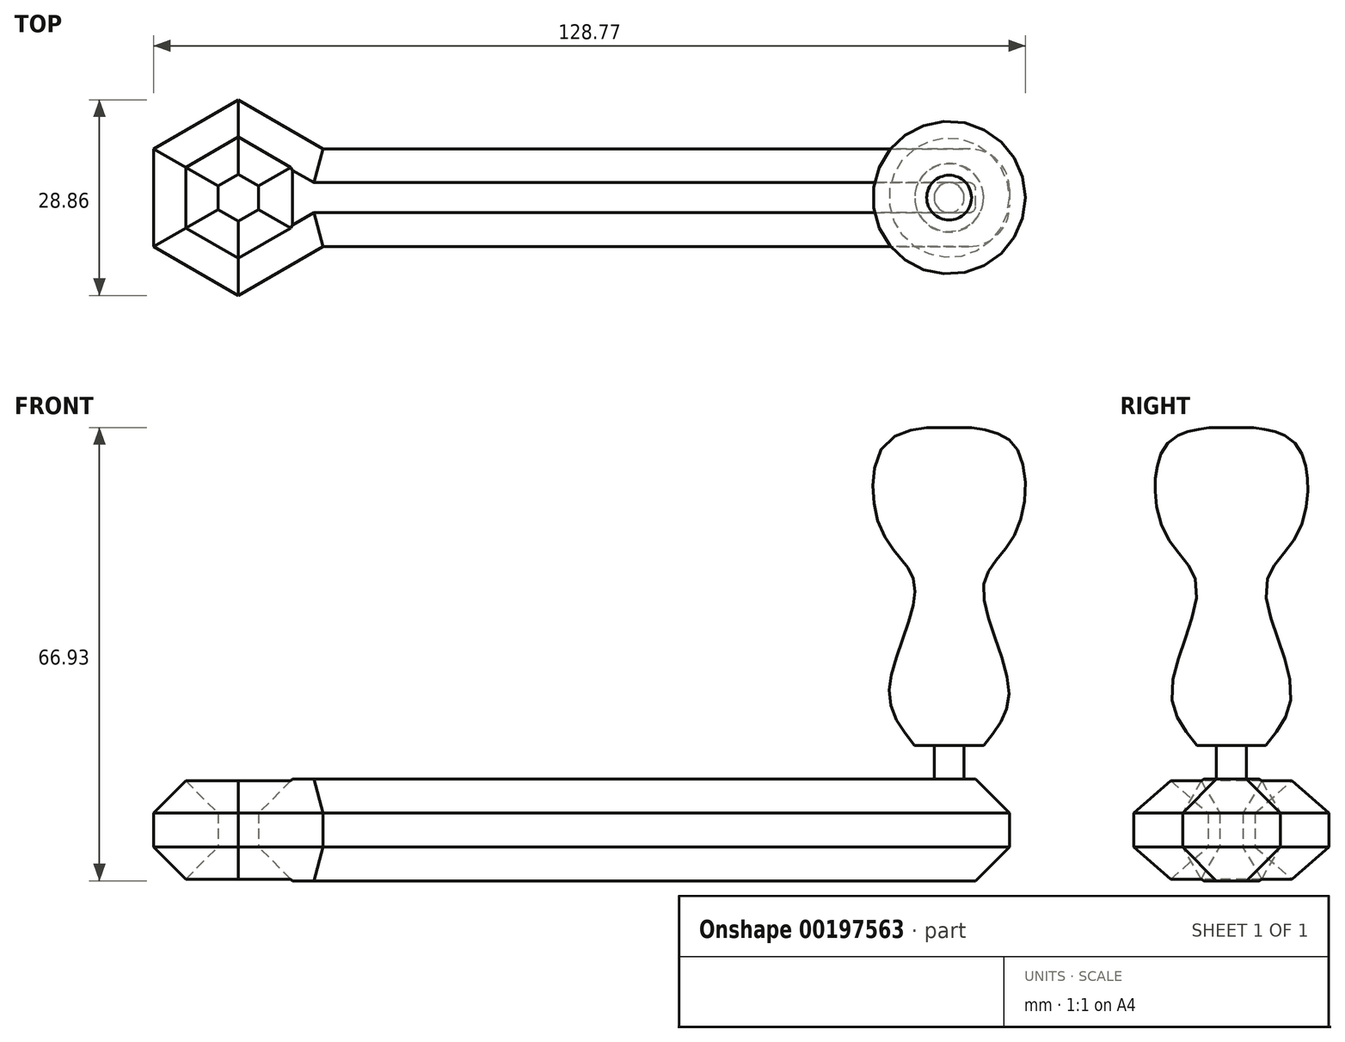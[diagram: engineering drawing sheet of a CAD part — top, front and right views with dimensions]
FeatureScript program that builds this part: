
annotation { "Feature Type Name" : "Feature", "Feature Type Description" : "" }
export const myFeature = defineFeature(function(context is Context, id is Id, definition is map)
    precondition{}
    {
        {
            var Q0;
            Q0=qCreatedBy(makeId("Top.planeOp"),FACE);
            var sketch = newSketch(context, id + "F0", { "sketchPlane" : qUnion([Q0])});
            skCircle(sketch, "E0.cCircle", {"center": v(0, 0) * mm, "radius": 3 * mm, "construction": true});
            skLineSegment(sketch, "E0.0", {"start": v(3, 1.73) * mm, "end": v(3, -1.73) * mm});
            skLineSegment(sketch, "E0.1", {"start": v(3, -1.73) * mm, "end": v(0, -3.46) * mm});
            skLineSegment(sketch, "E0.2", {"start": v(0, -3.46) * mm, "end": v(-3, -1.73) * mm});
            skLineSegment(sketch, "E0.3", {"start": v(-3, -1.73) * mm, "end": v(-3, 1.73) * mm});
            skLineSegment(sketch, "E0.4", {"start": v(-3, 1.73) * mm, "end": v(0, 3.46) * mm});
            skLineSegment(sketch, "E0.5", {"start": v(0, 3.46) * mm, "end": v(3, 1.73) * mm});
            skPoint(sketch, "E0.0.midPoint", {"position": v(3, 0) * mm});
            skCircle(sketch, "E1.cCircle", {"center": v(0, 0) * mm, "radius": 12.5 * mm, "construction": true});
            skLineSegment(sketch, "E1.0", {"start": v(12.5, 7.22) * mm, "end": v(12.5, -7.22) * mm});
            skLineSegment(sketch, "E1.1", {"start": v(12.5, -7.22) * mm, "end": v(0, -14.43) * mm});
            skLineSegment(sketch, "E1.2", {"start": v(0, -14.43) * mm, "end": v(-12.5, -7.22) * mm});
            skLineSegment(sketch, "E1.3", {"start": v(-12.5, -7.22) * mm, "end": v(-12.5, 7.22) * mm});
            skLineSegment(sketch, "E1.4", {"start": v(-12.5, 7.22) * mm, "end": v(0, 14.43) * mm});
            skLineSegment(sketch, "E1.5", {"start": v(0, 14.43) * mm, "end": v(12.5, 7.22) * mm});
            skPoint(sketch, "E1.0.midPoint", {"position": v(12.5, 0) * mm});
            skLineSegment(sketch, "E2.bottom", {"start": v(12.5, -7.22) * mm, "end": v(113.92, -7.22) * mm});
            skLineSegment(sketch, "E2.top", {"start": v(12.5, 7.22) * mm, "end": v(113.92, 7.22) * mm});
            skLineSegment(sketch, "E2.left", {"start": v(12.5, -7.22) * mm, "end": v(12.5, 7.22) * mm});
            skLineSegment(sketch, "E2.right", {"start": v(113.92, -7.22) * mm, "end": v(113.92, 7.22) * mm});
            skSolve(sketch);
        }
        {
            var Q0;
            Q0=makeQuery(id+"F0.imprint","IMPRINT",FACE,{"disambiguationData":[TD([[makeQuery(id+"F0.imprint","IMPRINT",EDGE,{"derivedFrom":sQuery(id+"F0.wireOp",EDGE,"E0.0")}),1.0]])]});
            var Q1;
            Q1=makeQuery(id+"F0.imprint","IMPRINT",FACE,{"disambiguationData":[TD([[makeQuery(id+"F0.imprint","IMPRINT",EDGE,{"derivedFrom":sQuery(id+"F0.wireOp",EDGE,"E2.bottom")}),1.0]])]});
            extrude(context, id + "F1", {"entities" : qUnion([Q0, Q1]), "depth" : 15 * mm});
        }
        {
            var Q0;
            Q0=makeQuery(id+"F1.opExtrude","SWEPT_EDGE",EDGE,{"disambiguationData":[OSD([sQuery(id+"F0.wireOp",EDGE,"E2.bottom"),sQuery(id+"F0.wireOp",EDGE,"E2.right")])]});
            var Q1;
            Q1=makeQuery(id+"F1.opExtrude","SWEPT_EDGE",EDGE,{"disambiguationData":[OSD([sQuery(id+"F0.wireOp",EDGE,"E2.top"),sQuery(id+"F0.wireOp",EDGE,"E2.right")])]});
            fillet(context, id + "F2", {"entities" : qUnion([Q0, Q1]), "radius" : 6 * mm, "tangentPropagation" : true, "allowEdgeOverflow" : false});
        }
        {
            var Q0;
            Q0=makeQuery(id+"F1.opExtrude","CAP_FACE",FACE,{"disambiguationData":[OSD([sQuery(id+"F0.wireOp",EDGE,"E0.0"),sQuery(id+"F0.wireOp",EDGE,"E0.1"),sQuery(id+"F0.wireOp",EDGE,"E0.2"),sQuery(id+"F0.wireOp",EDGE,"E0.3"),sQuery(id+"F0.wireOp",EDGE,"E0.4"),sQuery(id+"F0.wireOp",EDGE,"E0.5"),sQuery(id+"F0.wireOp",EDGE,"E1.1"),sQuery(id+"F0.wireOp",EDGE,"E1.2"),sQuery(id+"F0.wireOp",EDGE,"E1.3"),sQuery(id+"F0.wireOp",EDGE,"E1.4"),sQuery(id+"F0.wireOp",EDGE,"E1.5"),sQuery(id+"F0.wireOp",EDGE,"E2.bottom"),sQuery(id+"F0.wireOp",EDGE,"E2.top"),sQuery(id+"F0.wireOp",EDGE,"E2.right")])],"isStart":false});
            var Q1;
            Q1=makeQuery(id+"F1.opExtrude","CAP_FACE",FACE,{"disambiguationData":[OSD([sQuery(id+"F0.wireOp",EDGE,"E0.0"),sQuery(id+"F0.wireOp",EDGE,"E0.1"),sQuery(id+"F0.wireOp",EDGE,"E0.2"),sQuery(id+"F0.wireOp",EDGE,"E0.3"),sQuery(id+"F0.wireOp",EDGE,"E0.4"),sQuery(id+"F0.wireOp",EDGE,"E0.5"),sQuery(id+"F0.wireOp",EDGE,"E1.1"),sQuery(id+"F0.wireOp",EDGE,"E1.2"),sQuery(id+"F0.wireOp",EDGE,"E1.3"),sQuery(id+"F0.wireOp",EDGE,"E1.4"),sQuery(id+"F0.wireOp",EDGE,"E1.5"),sQuery(id+"F0.wireOp",EDGE,"E2.bottom"),sQuery(id+"F0.wireOp",EDGE,"E2.top"),sQuery(id+"F0.wireOp",EDGE,"E2.right")])],"isStart":true});
            chamfer(context, id + "F3", {"entities" : qUnion([Q0, Q1]), "width" : 5 * mm, "tangentPropagation" : true});
        }
        {
            var Q0;
            Q0=makeQuery(id+"F1.opExtrude","CAP_FACE",FACE,{"disambiguationData":[OSD([sQuery(id+"F0.wireOp",EDGE,"E0.0"),sQuery(id+"F0.wireOp",EDGE,"E0.1"),sQuery(id+"F0.wireOp",EDGE,"E0.2"),sQuery(id+"F0.wireOp",EDGE,"E0.3"),sQuery(id+"F0.wireOp",EDGE,"E0.4"),sQuery(id+"F0.wireOp",EDGE,"E0.5"),sQuery(id+"F0.wireOp",EDGE,"E1.1"),sQuery(id+"F0.wireOp",EDGE,"E1.2"),sQuery(id+"F0.wireOp",EDGE,"E1.3"),sQuery(id+"F0.wireOp",EDGE,"E1.4"),sQuery(id+"F0.wireOp",EDGE,"E1.5"),sQuery(id+"F0.wireOp",EDGE,"E2.bottom"),sQuery(id+"F0.wireOp",EDGE,"E2.top"),sQuery(id+"F0.wireOp",EDGE,"E2.right")])],"isStart":false});
            var sketch = newSketch(context, id + "F4", { "sketchPlane" : qUnion([Q0])});
            skCircle(sketch, "E3", {"center": v(105, 0) * mm, "radius": 2.22 * mm});
            skSolve(sketch);
        }
        {
            var Q0;
            Q0 = qSketchRegion(id + "F4", true);
            extrude(context, id + "F5", {"entities" : qUnion([Q0]), "operationType" : NewBodyOperationType.ADD, "depth" : 5 * mm});
        }
        {
            var Q0;
            Q0=qCreatedBy(makeId("Front.planeOp"),FACE);
            var sketch = newSketch(context, id + "F6", { "sketchPlane" : qUnion([Q0])});
            skLineSegment(sketch, "E4", {"start": v(0, 0) * mm, "end": v(0, 20) * mm, "construction": true});
            skLineSegment(sketch, "E5", {"start": v(0, 20) * mm, "end": v(105, 20) * mm, "construction": true});
            skLineSegment(sketch, "E6", {"start": v(105, 66.93) * mm, "end": v(105, 20) * mm});
            skLineSegment(sketch, "E7", {"start": v(105, 20) * mm, "end": v(110.08, 20) * mm});
            skLineSegment(sketch, "E8", {"start": v(105, 66.93) * mm, "end": v(108.3, 66.93) * mm});
            skFitSpline(sketch, "E9", {"points": [v(110.08, 20) * mm, v(113.83, 28.24) * mm, v(110.08, 43.52) * mm, v(114.82, 51.31) * mm, v(114.91, 63.93) * mm, v(108.3, 66.93) * mm], "startDerivative": vector(31.74, 38.28) * mm, "endDerivative": vector(-46.8, 7.32) * mm});
            skSolve(sketch);
        }
        {
            var Q0;
            Q0=makeQuery(id+"F6.imprint","IMPRINT",FACE,{"disambiguationData":[TD([[makeQuery(id+"F6.imprint","IMPRINT",EDGE,{"derivedFrom":sQuery(id+"F6.wireOp",EDGE,"E6")}),1.0]])]});
            var Q1;
            Q1=sQuery(id+"F6.wireOp",EDGE,"E6");
            revolve(context, id + "F7", {"operationType" : NewBodyOperationType.ADD, "entities" : qUnion([Q0]), "axis" : qUnion([Q1]), "revolveType" : RevolveType.FULL});
        }
    });
